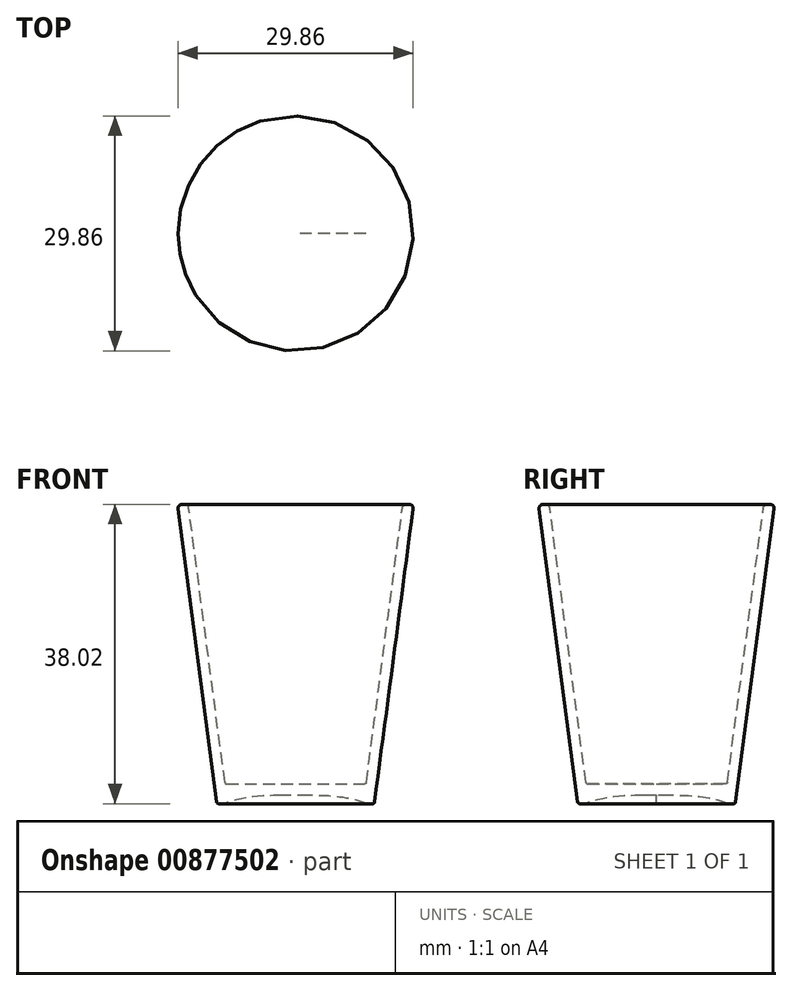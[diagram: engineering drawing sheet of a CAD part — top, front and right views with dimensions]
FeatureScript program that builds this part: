
annotation { "Feature Type Name" : "Feature", "Feature Type Description" : "" }
export const myFeature = defineFeature(function(context is Context, id is Id, definition is map)
    precondition{}
    {
        {
            var Q0;
            Q0=qCreatedBy(makeId("Front.planeOp"),FACE);
            var sketch = newSketch(context, id + "F0", { "sketchPlane" : qUnion([Q0])});
            skLineSegment(sketch, "E0", {"start": v(10, 0) * mm, "end": v(15, 38.02) * mm});
            skLineSegment(sketch, "E1", {"start": v(10, 0) * mm, "end": v(9, 0) * mm});
            skFitSpline(sketch, "E2", {"points": [v(9, 0) * mm, v(0, 1) * mm], "startDerivative": vector(-8.2, 3.58) * mm, "endDerivative": vector(-4.11, -0.18) * mm});
            skLineSegment(sketch, "E3", {"start": v(0, 1) * mm, "end": v(0, 2.5) * mm});
            skLineSegment(sketch, "E4", {"start": v(0, 2.5) * mm, "end": v(8.96, 2.5) * mm});
            skLineSegment(sketch, "E5", {"start": v(8.96, 2.5) * mm, "end": v(13.63, 38.02) * mm});
            skLineSegment(sketch, "E6", {"start": v(13.63, 38.02) * mm, "end": v(15, 38.02) * mm});
            skSolve(sketch);
        }
        {
            var Q0;
            Q0=makeQuery(id+"F0.imprint","IMPRINT",FACE,{"disambiguationData":[TD([[makeQuery(id+"F0.imprint","IMPRINT",EDGE,{"derivedFrom":sQuery(id+"F0.wireOp",EDGE,"E0")}),1.0]])]});
            var Q1;
            Q1=sQuery(id+"F0.wireOp",EDGE,"E3");
            revolve(context, id + "F1", {"surfaceOperationType" : NewSurfaceOperationType.NEW, "entities" : qUnion([Q0]), "axis" : qUnion([Q1]), "revolveType" : RevolveType.FULL});
        }
        {
            var Q0;
            Q0=makeQuery(id+"F1.opRevolve","SWEPT_EDGE",EDGE,{"disambiguationData":[OSD([sQuery(id+"F0.wireOp",EDGE,"E5"),sQuery(id+"F0.wireOp",EDGE,"E6")])]});
            var Q1;
            Q1=makeQuery(id+"F1.opRevolve","SWEPT_EDGE",EDGE,{"disambiguationData":[OSD([sQuery(id+"F0.wireOp",EDGE,"E0"),sQuery(id+"F0.wireOp",EDGE,"E6")])]});
            fillet(context, id + "F2", {"entities" : qUnion([Q0, Q1]), "radius" : .5 * mm, "tangentPropagation" : true, "allowEdgeOverflow" : false});
        }
        {
            var Q0;
            Q0=makeQuery(id+"F1.opRevolve","SWEPT_EDGE",EDGE,{"disambiguationData":[OSD([sQuery(id+"F0.wireOp",EDGE,"E4"),sQuery(id+"F0.wireOp",EDGE,"E5")])]});
            var Q1;
            Q1=makeQuery(id+"F1.opRevolve","SWEPT_EDGE",EDGE,{"disambiguationData":[OSD([sQuery(id+"F0.wireOp",EDGE,"E1"),sQuery(id+"F0.wireOp",EDGE,"E2")])]});
            var Q2;
            Q2=makeQuery(id+"F1.opRevolve","SWEPT_EDGE",EDGE,{"disambiguationData":[OSD([sQuery(id+"F0.wireOp",EDGE,"E0"),sQuery(id+"F0.wireOp",EDGE,"E1")])]});
            fillet(context, id + "F3", {"entities" : qUnion([Q0, Q1, Q2]), "radius" : .25 * mm, "tangentPropagation" : true, "allowEdgeOverflow" : false});
        }
    });
